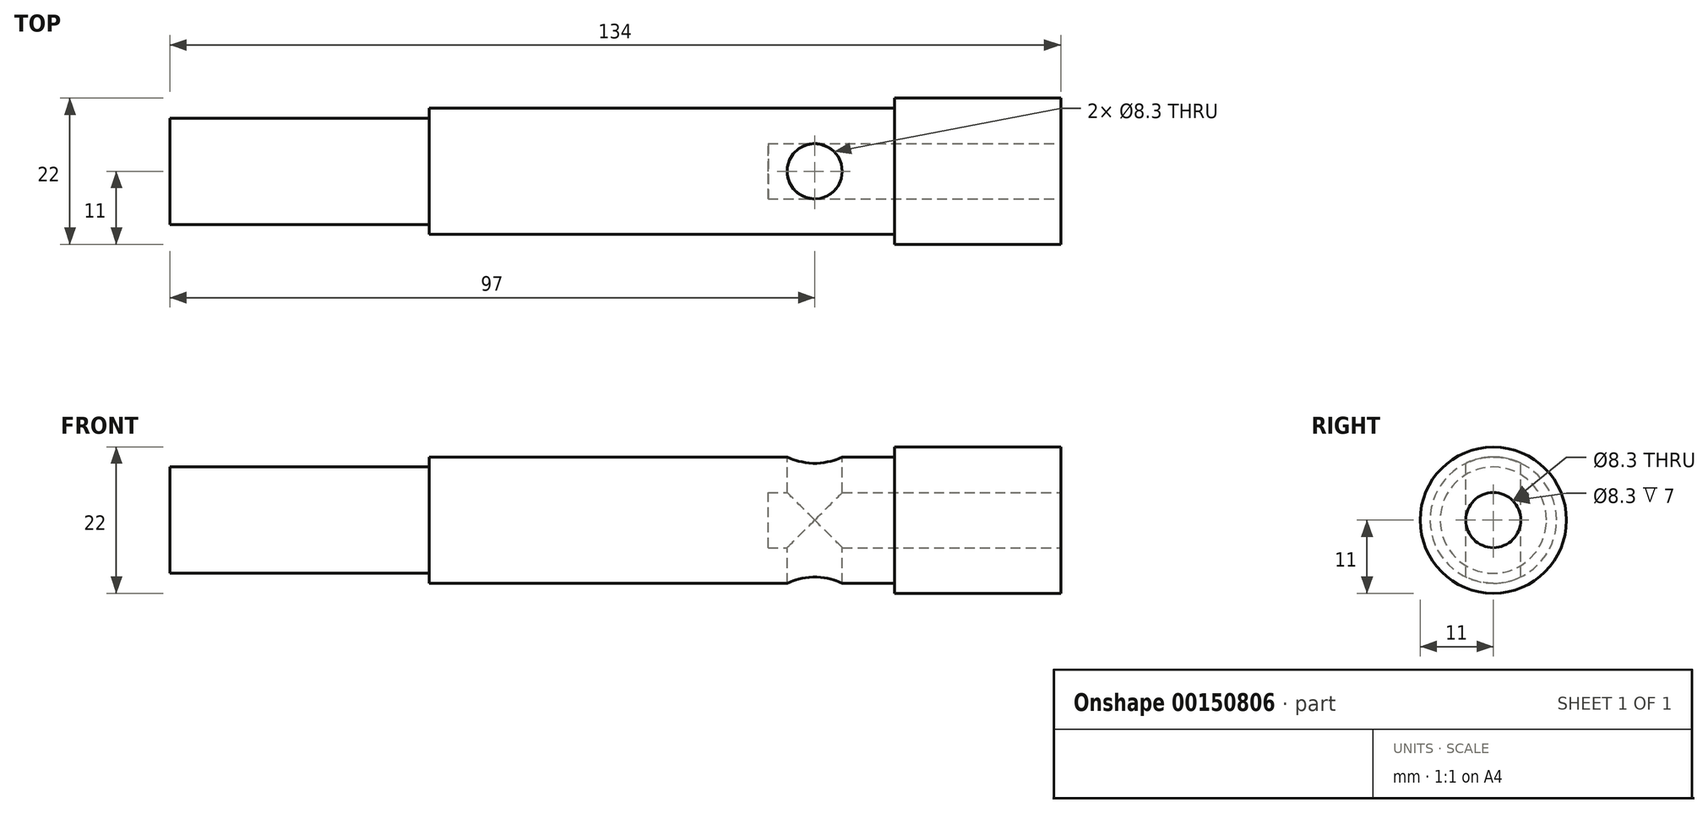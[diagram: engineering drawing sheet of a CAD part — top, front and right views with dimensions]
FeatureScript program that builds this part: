
annotation { "Feature Type Name" : "Feature", "Feature Type Description" : "" }
export const myFeature = defineFeature(function(context is Context, id is Id, definition is map)
    precondition{}
    {
        {
            var Q0;
            Q0=qCreatedBy(makeId("Right.planeOp"),FACE);
            var sketch = newSketch(context, id + "F0", { "sketchPlane" : qUnion([Q0])});
            skCircle(sketch, "E0", {"center": v(0, 0) * mm, "radius": 11 * mm});
            skSolve(sketch);
        }
        {
            var Q0;
            Q0=makeQuery(id+"F0.imprint","IMPRINT",FACE,{"disambiguationData":[TD([[makeQuery(id+"F0.imprint","IMPRINT",EDGE,{"derivedFrom":sQuery(id+"F0.wireOp",EDGE,"E0")}),1.0]])]});
            extrude(context, id + "F1", {"entities" : qUnion([Q0]), "depth" : 134 * mm, "symmetric" : true});
        }
        {
            var Q0;
            Q0=makeQuery(id+"F1.opExtrude","CAP_FACE",FACE,{"disambiguationData":[OSD([sQuery(id+"F0.wireOp",EDGE,"E0")])],"isStart":false});
            cPlane(context, id + "F2", {"entities" : qUnion([Q0]), "cplaneType" : CPlaneType.OFFSET, "offset" : 25 * mm, "oppositeDirection" : true, "width" : 150 * mm, "height" : 150 * mm});
        }
        {
            var Q0;
            Q0=qCreatedBy(id+"F2.planeOp",FACE);
            var sketch = newSketch(context, id + "F3", { "sketchPlane" : qUnion([Q0])});
            skCircle(sketch, "E1", {"center": v(0, 0) * mm, "radius": 9.5 * mm});
            skCircle(sketch, "E2", {"center": v(0, 0) * mm, "radius": 11 * mm});
            skSolve(sketch);
        }
        {
            var Q0;
            Q0=makeQuery(id+"F3.imprint","IMPRINT",FACE,{"disambiguationData":[TD([[makeQuery(id+"F3.imprint","IMPRINT",EDGE,{"derivedFrom":sQuery(id+"F3.wireOp",EDGE,"E1")}),-1.0]])]});
            extrude(context, id + "F4", {"entities" : qUnion([Q0]), "operationType" : NewBodyOperationType.REMOVE, "oppositeDirection" : true, "depth" : 70 * mm});
        }
        {
            var Q0;
            Q0=makeQuery(id+"F4.boolean.opBoolean","COPY",FACE,{"derivedFrom":makeQuery(id+"F4.opExtrude","CAP_FACE",FACE,{"disambiguationData":[OSD([sQuery(id+"F3.wireOp",EDGE,"E1"),sQuery(id+"F3.wireOp",EDGE,"E2")])],"isStart":false})});
            cPlane(context, id + "F5", {"entities" : qUnion([Q0]), "cplaneType" : CPlaneType.OFFSET, "offset" : 0 * mm, "width" : 150 * mm, "height" : 150 * mm});
        }
        {
            var Q0;
            Q0=qCreatedBy(id+"F5.planeOp",FACE);
            var sketch = newSketch(context, id + "F6", { "sketchPlane" : qUnion([Q0])});
            skCircle(sketch, "E3", {"center": v(0, 0) * mm, "radius": 8 * mm});
            skCircle(sketch, "E4", {"center": v(0, 0) * mm, "radius": 11 * mm});
            skSolve(sketch);
        }
        {
            var Q0;
            Q0=makeQuery(id+"F6.imprint","IMPRINT",FACE,{"disambiguationData":[TD([[makeQuery(id+"F6.imprint","IMPRINT",EDGE,{"derivedFrom":sQuery(id+"F6.wireOp",EDGE,"E3")}),-1.0]])]});
            extrude(context, id + "F7", {"entities" : qUnion([Q0]), "operationType" : NewBodyOperationType.REMOVE, "endBound" : BoundingType.THROUGH_ALL, "oppositeDirection" : true, "depth" : 25 * mm});
        }
        {
            var Q0;
            Q0=makeQuery(id+"F1.opExtrude","CAP_FACE",FACE,{"disambiguationData":[OSD([sQuery(id+"F0.wireOp",EDGE,"E0")])],"isStart":false});
            var sketch = newSketch(context, id + "F8", { "sketchPlane" : qUnion([Q0])});
            skCircle(sketch, "E5", {"center": v(0, 0) * mm, "radius": 4.15 * mm});
            skSolve(sketch);
        }
        {
            var Q0;
            Q0=makeQuery(id+"F8.imprint","IMPRINT",FACE,{"disambiguationData":[TD([[makeQuery(id+"F8.imprint","IMPRINT",EDGE,{"derivedFrom":sQuery(id+"F8.wireOp",EDGE,"E5")}),1.0]])]});
            extrude(context, id + "F9", {"entities" : qUnion([Q0]), "operationType" : NewBodyOperationType.REMOVE, "oppositeDirection" : true, "depth" : 44 * mm});
        }
        {
            var Q0;
            Q0=qCreatedBy(makeId("Top.planeOp"),FACE);
            cPlane(context, id + "F10", {"entities" : qUnion([Q0]), "cplaneType" : CPlaneType.OFFSET, "offset" : 9.5 * mm, "width" : 150 * mm, "height" : 150 * mm});
        }
        {
            var Q0;
            Q0=qCreatedBy(id+"F10.planeOp",FACE);
            var sketch = newSketch(context, id + "F11", { "sketchPlane" : qUnion([Q0])});
            skCircle(sketch, "E6", {"center": v(30, 0) * mm, "radius": 4.15 * mm});
            skSolve(sketch);
        }
        {
            var Q0;
            Q0=makeQuery(id+"F11.imprint","IMPRINT",FACE,{"disambiguationData":[TD([[makeQuery(id+"F11.imprint","IMPRINT",EDGE,{"derivedFrom":sQuery(id+"F11.wireOp",EDGE,"E6")}),1.0]])]});
            extrude(context, id + "F12", {"entities" : qUnion([Q0]), "operationType" : NewBodyOperationType.REMOVE, "endBound" : BoundingType.THROUGH_ALL, "oppositeDirection" : true, "depth" : 25 * mm});
        }
    });
